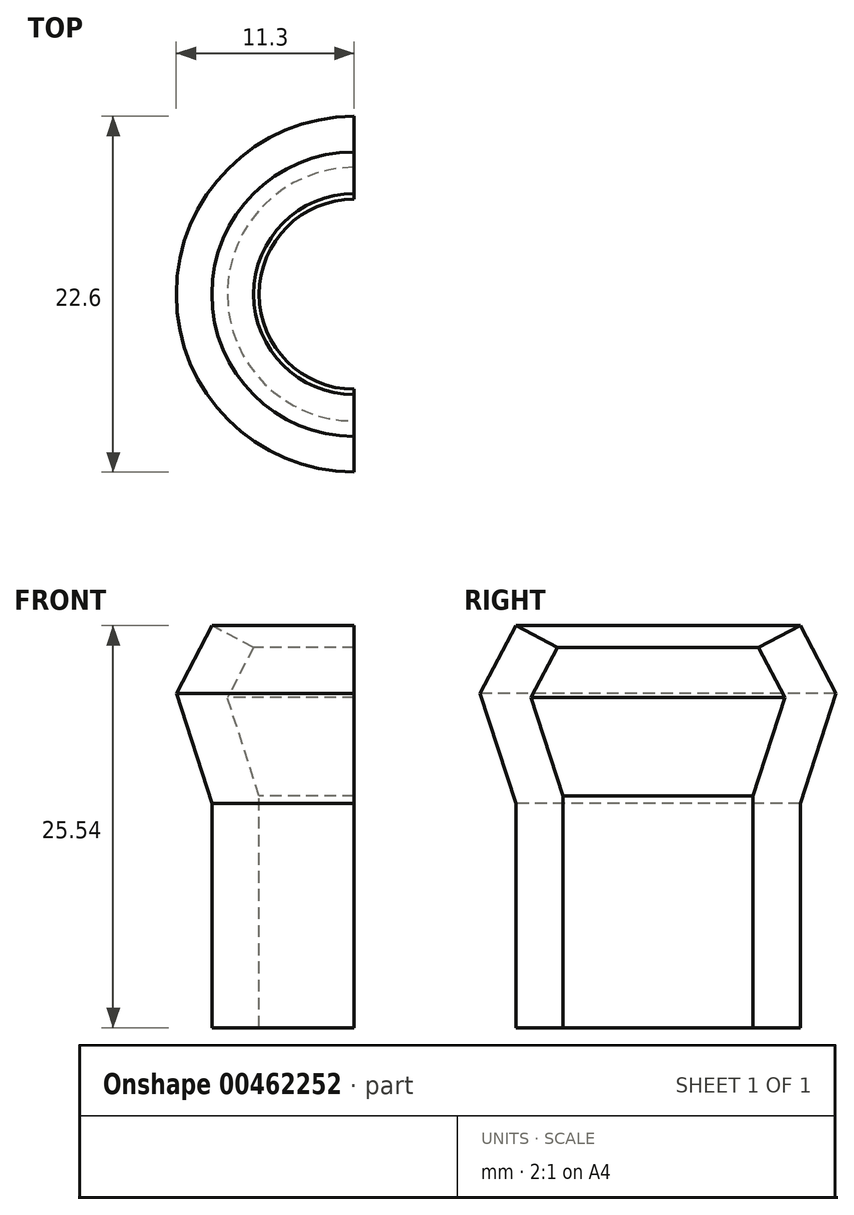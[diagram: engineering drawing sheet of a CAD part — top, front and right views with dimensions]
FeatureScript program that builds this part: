
annotation { "Feature Type Name" : "Feature", "Feature Type Description" : "" }
export const myFeature = defineFeature(function(context is Context, id is Id, definition is map)
    precondition{}
    {
        {
            var Q0;
            Q0=qCreatedBy(makeId("Front.planeOp"),FACE);
            var sketch = newSketch(context, id + "F0", { "sketchPlane" : qUnion([Q0])});
            skLineSegment(sketch, "E0", {"start": v(-24.18, 40.34) * mm, "end": v(-24.18, 13.9) * mm});
            skLineSegment(sketch, "E1", {"start": v(-33.22, 40.34) * mm, "end": v(-35.48, 36.04) * mm});
            skLineSegment(sketch, "E2", {"start": v(-35.48, 36.04) * mm, "end": v(-33.22, 29.04) * mm});
            skLineSegment(sketch, "E3", {"start": v(-33.22, 29.04) * mm, "end": v(-33.22, 14.8) * mm});
            skLineSegment(sketch, "E4.0", {"start": v(-30.22, 29.5) * mm, "end": v(-30.22, 14.8) * mm});
            skLineSegment(sketch, "E4.1", {"start": v(-32.23, 35.76) * mm, "end": v(-30.22, 29.5) * mm});
            skLineSegment(sketch, "E4.2", {"start": v(-30.56, 38.94) * mm, "end": v(-32.23, 35.76) * mm});
            skLineSegment(sketch, "E5", {"start": v(-33.22, 40.34) * mm, "end": v(-30.56, 38.94) * mm});
            skLineSegment(sketch, "E6", {"start": v(-33.22, 14.8) * mm, "end": v(-30.22, 14.8) * mm});
            skSolve(sketch);
        }
        {
            var Q0;
            Q0 = qSketchRegion(id + "F0", true);
            var Q1;
            Q1=sQuery(id+"F0.wireOp",EDGE,"E0");
            revolve(context, id + "F1", {"entities" : qUnion([Q0]), "axis" : qUnion([Q1]), "revolveType" : RevolveType.SYMMETRIC, "angle" : 180 * degree});
        }
    });
